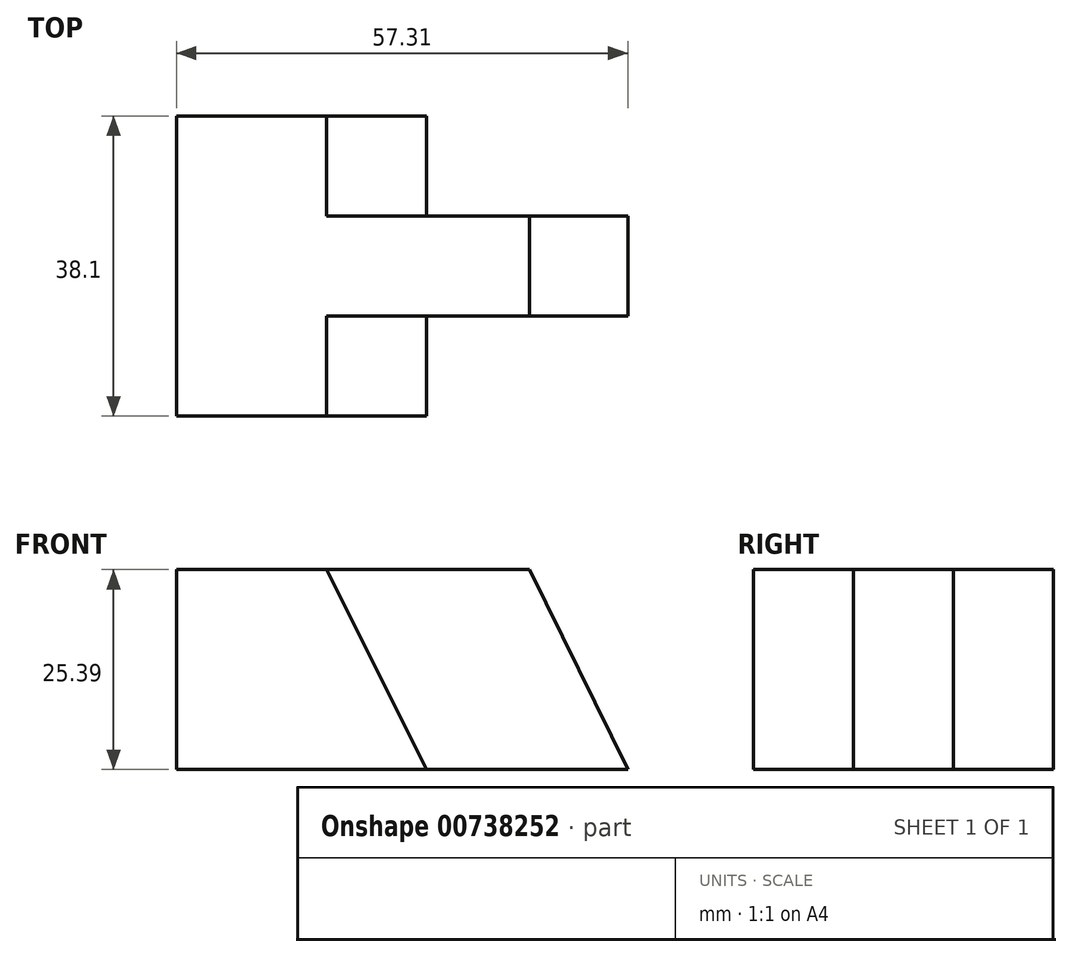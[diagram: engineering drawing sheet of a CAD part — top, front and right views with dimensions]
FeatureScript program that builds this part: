
annotation { "Feature Type Name" : "Feature", "Feature Type Description" : "" }
export const myFeature = defineFeature(function(context is Context, id is Id, definition is map)
    precondition{}
    {
        {
            var Q0;
            Q0=qCreatedBy(makeId("Front.planeOp"),FACE);
            var sketch = newSketch(context, id + "F0", { "sketchPlane" : qUnion([Q0])});
            skLineSegment(sketch, "E0", {"start": v(-2.41, 0) * mm, "end": v(54.9, 0) * mm});
            skLineSegment(sketch, "E1", {"start": v(-2.41, 0) * mm, "end": v(-2.41, 25.4) * mm});
            skLineSegment(sketch, "E2", {"start": v(-2.41, 25.4) * mm, "end": v(54.9, 25.4) * mm});
            skLineSegment(sketch, "E3", {"start": v(54.9, 25.4) * mm, "end": v(54.9, 0) * mm});
            skSolve(sketch);
        }
        {
            var Q0;
            Q0=makeQuery(id+"F0.imprint","IMPRINT",FACE,{"disambiguationData":[TD([[makeQuery(id+"F0.imprint","IMPRINT",EDGE,{"derivedFrom":sQuery(id+"F0.wireOp",EDGE,"E0")}),1.0]])]});
            extrude(context, id + "F1", {"entities" : qUnion([Q0]), "depth" : 38.1 * mm, "offsetDistance" : 25.4 * mm});
        }
        {
            var Q0;
            Q0=makeQuery(id+"F1.opExtrude","CAP_FACE",FACE,{"disambiguationData":[OSD([sQuery(id+"F0.wireOp",EDGE,"E0"),sQuery(id+"F0.wireOp",EDGE,"E1"),sQuery(id+"F0.wireOp",EDGE,"E2"),sQuery(id+"F0.wireOp",EDGE,"E3")])],"isStart":false});
            var sketch = newSketch(context, id + "F2", { "sketchPlane" : qUnion([Q0])});
            skLineSegment(sketch, "E4", {"start": v(-2.41, 25.4) * mm, "end": v(16.64, 25.4) * mm});
            skLineSegment(sketch, "E5", {"start": v(16.64, 25.4) * mm, "end": v(29.37, 0) * mm});
            skSolve(sketch);
        }
        {
            var Q0;
            {var subQ0=sQuery(id+"F2.wireOp",EDGE,"E5");Q0=makeQuery(id+"F2.imprint","IMPRINT",FACE,{"disambiguationData":[TD([[makeQuery(id+"F2.imprint","IMPRINT",EDGE,{"derivedFrom":subQ0}),1.0]])]});}
            extrude(context, id + "F3", {"entities" : qUnion([Q0]), "operationType" : NewBodyOperationType.REMOVE, "oppositeDirection" : true, "depth" : 12.7 * mm, "offsetDistance" : 25.4 * mm});
        }
        {
            var Q0;
            Q0=makeQuery(id+"F3.boolean.opBoolean","COPY",FACE,{"derivedFrom":makeQuery(id+"F3.opExtrude","CAP_FACE",FACE,{"disambiguationData":[OSD([sQuery(id+"F0.wireOp",EDGE,"E0"),sQuery(id+"F0.wireOp",EDGE,"E2"),sQuery(id+"F0.wireOp",EDGE,"E3"),sQuery(id+"F2.wireOp",EDGE,"E5")])],"isStart":false})});
            var sketch = newSketch(context, id + "F4", { "sketchPlane" : qUnion([Q0])});
            skLineSegment(sketch, "E6", {"start": v(54.9, 25.4) * mm, "end": v(42.42, 25.4) * mm});
            skLineSegment(sketch, "E7", {"start": v(42.42, 25.4) * mm, "end": v(54.9, 0) * mm});
            skSolve(sketch);
        }
        {
            var Q0;
            Q0=makeQuery(id+"F4.imprint","IMPRINT",FACE,{"disambiguationData":[TD([[makeQuery(id+"F4.imprint","IMPRINT",EDGE,{"derivedFrom":sQuery(id+"F4.wireOp",EDGE,"E6")}),-1.0]])]});
            extrude(context, id + "F5", {"entities" : qUnion([Q0]), "operationType" : NewBodyOperationType.REMOVE, "oppositeDirection" : true, "depth" : 12.7 * mm, "offsetDistance" : 25.4 * mm});
        }
        {
            var Q0;
            Q0=makeQuery(id+"F1.opExtrude","CAP_FACE",FACE,{"disambiguationData":[OSD([sQuery(id+"F0.wireOp",EDGE,"E0"),sQuery(id+"F0.wireOp",EDGE,"E1"),sQuery(id+"F0.wireOp",EDGE,"E2"),sQuery(id+"F0.wireOp",EDGE,"E3")])],"isStart":true});
            var sketch = newSketch(context, id + "F6", { "sketchPlane" : qUnion([Q0])});
            skLineSegment(sketch, "E8", {"start": v(2.41, 25.4) * mm, "end": v(-16.67, 25.4) * mm});
            skLineSegment(sketch, "E9", {"start": v(-54.9, 0) * mm, "end": v(-42.14, 0) * mm});
            skLineSegment(sketch, "E10", {"start": v(-37.43, 42.31) * mm, "end": v(-37.58, 40.92) * mm});
            skLineSegment(sketch, "E11", {"start": v(-42.14, 0) * mm, "end": v(-29.32, 0) * mm});
            skLineSegment(sketch, "E12", {"start": v(-16.67, 25.4) * mm, "end": v(-29.32, 0) * mm});
            skSolve(sketch);
        }
        {
            var Q0;
            Q0=makeQuery(id+"F6.imprint","IMPRINT",FACE,{"disambiguationData":[TD([[makeQuery(id+"F6.imprint","IMPRINT",EDGE,{"derivedFrom":sQuery(id+"F6.wireOp",EDGE,"E9")}),-1.0]])]});
            extrude(context, id + "F7", {"entities" : qUnion([Q0]), "operationType" : NewBodyOperationType.REMOVE, "oppositeDirection" : true, "depth" : 12.7 * mm, "offsetDistance" : 25.4 * mm});
        }
    });
